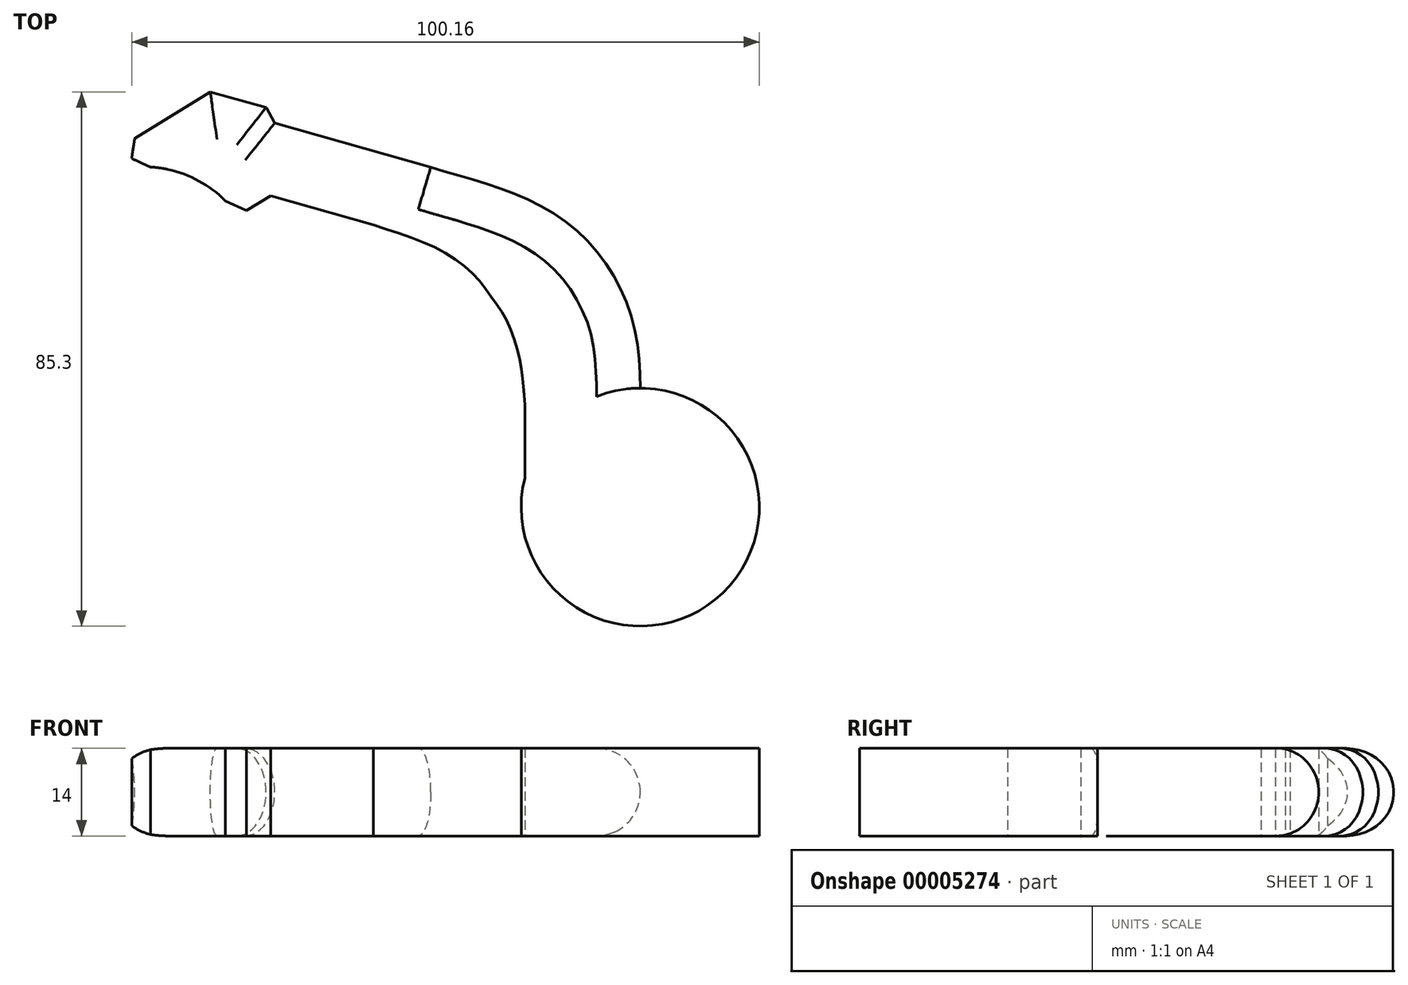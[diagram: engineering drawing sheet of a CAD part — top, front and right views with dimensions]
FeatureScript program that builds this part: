
annotation { "Feature Type Name" : "Feature", "Feature Type Description" : "" }
export const myFeature = defineFeature(function(context is Context, id is Id, definition is map)
    precondition{}
    {
        {
            var Q0;
            Q0=qCreatedBy(makeId("Top.planeOp"),FACE);
            var sketch = newSketch(context, id + "F0", { "sketchPlane" : qUnion([Q0])});
            skArc(sketch, "E0", {"start": v(-18.43, 4.63) * mm, "mid": v(11.68, -14.98) * mm, "end": v(0, 19) * mm});
            skLineSegment(sketch, "E1", {"start": v(-80.7, 58.88) * mm, "end": v(-68.63, 66.3) * mm});
            skLineSegment(sketch, "E2", {"start": v(-68.63, 66.3) * mm, "end": v(-59.7, 63.82) * mm});
            skLineSegment(sketch, "E3", {"start": v(-59.7, 63.82) * mm, "end": v(-58.33, 61.35) * mm});
            skLineSegment(sketch, "E4", {"start": v(-58.33, 61.35) * mm, "end": v(-33.44, 54.27) * mm});
            skLineSegment(sketch, "E5", {"start": v(0, 19) * mm, "end": v(0, 0) * mm});
            skLineSegment(sketch, "E6", {"start": v(-80.7, 58.88) * mm, "end": v(-81.16, 55.67) * mm});
            skLineSegment(sketch, "E7", {"start": v(-81.16, 55.67) * mm, "end": v(-78.15, 54.3) * mm});
            skLineSegment(sketch, "E8", {"start": v(-62.83, 47.38) * mm, "end": v(-58.99, 49.7) * mm});
            skLineSegment(sketch, "E9", {"start": v(-58.99, 49.7) * mm, "end": v(-42.58, 45.07) * mm});
            skLineSegment(sketch, "E10", {"start": v(-18.43, 16.3) * mm, "end": v(-18.43, 4.63) * mm});
            skArc(sketch, "E11", {"start": v(-66.23, 48.91) * mm, "mid": v(-71.7, 52.7) * mm, "end": v(-78.15, 54.3) * mm});
            skFitSpline(sketch, "E12", {"points": [v(-33.44, 54.27) * mm, v(-22.87, 51.08) * mm, v(-13.66, 46.8) * mm, v(-7.33, 41.3) * mm, v(-3.54, 35.62) * mm, v(-1.16, 29.53) * mm, v(0, 19) * mm], "startDerivative": vector(52.87, -16) * mm, "endDerivative": vector(0, -65.65) * mm});
            skPoint(sketch, "E13.orphan", {"position": v(0, 44.75) * mm});
            skFitSpline(sketch, "E14", {"points": [v(-42.58, 45.07) * mm, v(-33.64, 41.87) * mm, v(-27.23, 37.76) * mm, v(-23.69, 33.48) * mm, v(-21.06, 29.29) * mm, v(-19.25, 23.53) * mm, v(-18.43, 16.3) * mm], "startDerivative": vector(46.77, -16.08) * mm, "endDerivative": vector(4.3, -61.62) * mm});
            skLineSegment(sketch, "E15.trimOffspring", {"start": v(-66.23, 48.91) * mm, "end": v(-62.83, 47.38) * mm});
            skPoint(sketch, "E16.orphan", {"position": v(-18.43, 0) * mm});
            skSolve(sketch);
        }
        {
            var Q0;
            Q0 = qSketchRegion(id + "F0", true);
            extrude(context, id + "F1", {"entities" : qUnion([Q0]), "depth" : 14 * mm});
        }
        {
            var Q0;
            Q0=makeQuery(id+"F1.opExtrude","CAP_EDGE",EDGE,{"disambiguationData":[OSD([sQuery(id+"F0.wireOp",EDGE,"E12")])],"isStart":false});
            var Q1;
            Q1=makeQuery(id+"F1.opExtrude","CAP_EDGE",EDGE,{"disambiguationData":[OSD([sQuery(id+"F0.wireOp",EDGE,"E1")])],"isStart":false});
            var Q2;
            Q2=makeQuery(id+"F1.opExtrude","CAP_EDGE",EDGE,{"disambiguationData":[OSD([sQuery(id+"F0.wireOp",EDGE,"E2")])],"isStart":false});
            var Q3;
            Q3=makeQuery(id+"F1.opExtrude","CAP_EDGE",EDGE,{"disambiguationData":[OSD([sQuery(id+"F0.wireOp",EDGE,"E3")])],"isStart":false});
            var Q4;
            Q4=makeQuery(id+"F1.opExtrude","CAP_EDGE",EDGE,{"disambiguationData":[OSD([sQuery(id+"F0.wireOp",EDGE,"E4")])],"isStart":false});
            var Q5;
            Q5=makeQuery(id+"F1.opExtrude","CAP_EDGE",EDGE,{"disambiguationData":[OSD([sQuery(id+"F0.wireOp",EDGE,"E12")])],"isStart":true});
            var Q6;
            Q6=makeQuery(id+"F1.opExtrude","CAP_EDGE",EDGE,{"disambiguationData":[OSD([sQuery(id+"F0.wireOp",EDGE,"E4")])],"isStart":true});
            var Q7;
            Q7=makeQuery(id+"F1.opExtrude","CAP_EDGE",EDGE,{"disambiguationData":[OSD([sQuery(id+"F0.wireOp",EDGE,"E3")])],"isStart":true});
            var Q8;
            Q8=makeQuery(id+"F1.opExtrude","CAP_EDGE",EDGE,{"disambiguationData":[OSD([sQuery(id+"F0.wireOp",EDGE,"E2")])],"isStart":true});
            var Q9;
            Q9=makeQuery(id+"F1.opExtrude","CAP_EDGE",EDGE,{"disambiguationData":[OSD([sQuery(id+"F0.wireOp",EDGE,"E1")])],"isStart":true});
            fillet(context, id + "F2", {"entities" : qUnion([Q0, Q1, Q2, Q3, Q4, Q5, Q6, Q7, Q8, Q9]), "radius" : 7 * mm, "tangentPropagation" : true, "allowEdgeOverflow" : false});
        }
    });
